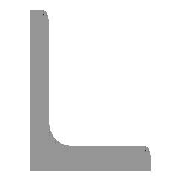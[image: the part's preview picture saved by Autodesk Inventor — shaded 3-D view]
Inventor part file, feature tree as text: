
AUTODESK INVENTOR PART (.ipt)
format: ipt  version: 2013 (Build 170138000, 138)  size: 129,024 bytes
history: native  units: mm (DEFAULTED — no unit token found)
features: other x4, plane x3, split x2, sketch x2
ambient origin geometry x8: Origin, YZ Plane, XZ Plane, XY Plane, X Axis, Y Axis, Z Axis, Center Point
bodies: Solid1 (feature_tree), Body (feature_tree)
feature tree (11):
  parser-record x1  (decoder bookkeeping rows leaked as tree rows — omitted from the tree; the rows remain in map.json)
  other  "Driven Length"
  other  "Start plane"
  other  "End plane"
  plane  "Work Plane4"
  split  "Split1"
  plane  "Work Plane5"
  split  "Split2"
  sketch  "Sketch3"  dims[d0=38.1mm]
  plane  "Work Plane3"
  sketch  "Sketch4"  dims[d1=38.1mm d2=4.7625mm d3=4.7625mm d4=1092.2mm d5=0.0mm d10=0.0mm d11=0.0mm d12=-0.0mm d13=1092.2mm d14=4.826mm d15=2.286mm d16=90.0deg d17=1092.2mm]
